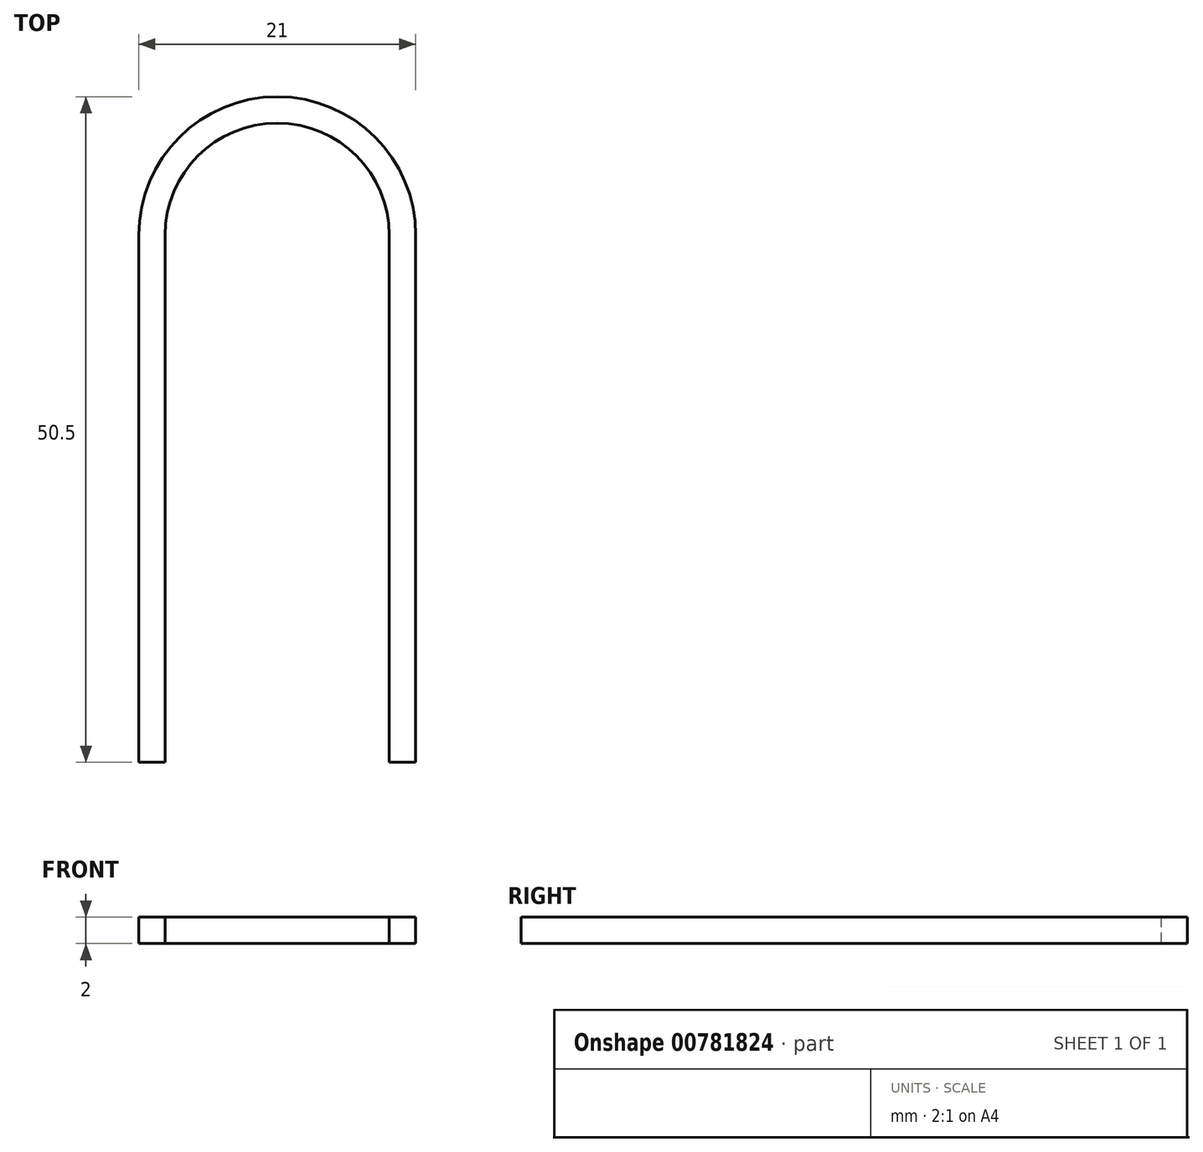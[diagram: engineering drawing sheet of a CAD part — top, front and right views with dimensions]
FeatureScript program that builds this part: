
annotation { "Feature Type Name" : "Feature", "Feature Type Description" : "" }
export const myFeature = defineFeature(function(context is Context, id is Id, definition is map)
    precondition{}
    {
        {
            var Q0;
            Q0=qCreatedBy(makeId("Top.planeOp"),FACE);
            var sketch = newSketch(context, id + "F0", { "sketchPlane" : qUnion([Q0])});
            skLineSegment(sketch, "E0", {"start": v(-8.5, 0) * mm, "end": v(8.5, 0) * mm, "construction": true});
            skPoint(sketch, "E1", {"position": v(0, 0) * mm});
            skLineSegment(sketch, "E2", {"start": v(-8.5, 0) * mm, "end": v(-8.5, 40) * mm});
            skArc(sketch, "E3", {"start": v(-8.5, 40) * mm, "mid": v(0, 48.5) * mm, "end": v(8.5, 40) * mm});
            skLineSegment(sketch, "E4", {"start": v(8.5, 0) * mm, "end": v(8.5, 40) * mm});
            skLineSegment(sketch, "E5.0", {"start": v(10.5, 0) * mm, "end": v(10.5, 40) * mm});
            skArc(sketch, "E5.1", {"start": v(-10.5, 40) * mm, "mid": v(0, 50.5) * mm, "end": v(10.5, 40) * mm});
            skLineSegment(sketch, "E5.2", {"start": v(-10.5, 0) * mm, "end": v(-10.5, 40) * mm});
            skLineSegment(sketch, "E6", {"start": v(-10.5, 0) * mm, "end": v(-8.5, 0) * mm});
            skLineSegment(sketch, "E7", {"start": v(8.5, 0) * mm, "end": v(10.5, 0) * mm});
            skSolve(sketch);
        }
        {
            var Q0;
            Q0=makeQuery(id+"F0.imprint","IMPRINT",FACE,{"disambiguationData":[TD([[makeQuery(id+"F0.imprint","IMPRINT",EDGE,{"derivedFrom":sQuery(id+"F0.wireOp",EDGE,"E2")}),1.0]])]});
            extrude(context, id + "F1", {"entities" : qUnion([Q0]), "depth" : 2 * mm, "offsetDistance" : 25 * mm, "symmetric" : true});
        }
    });
